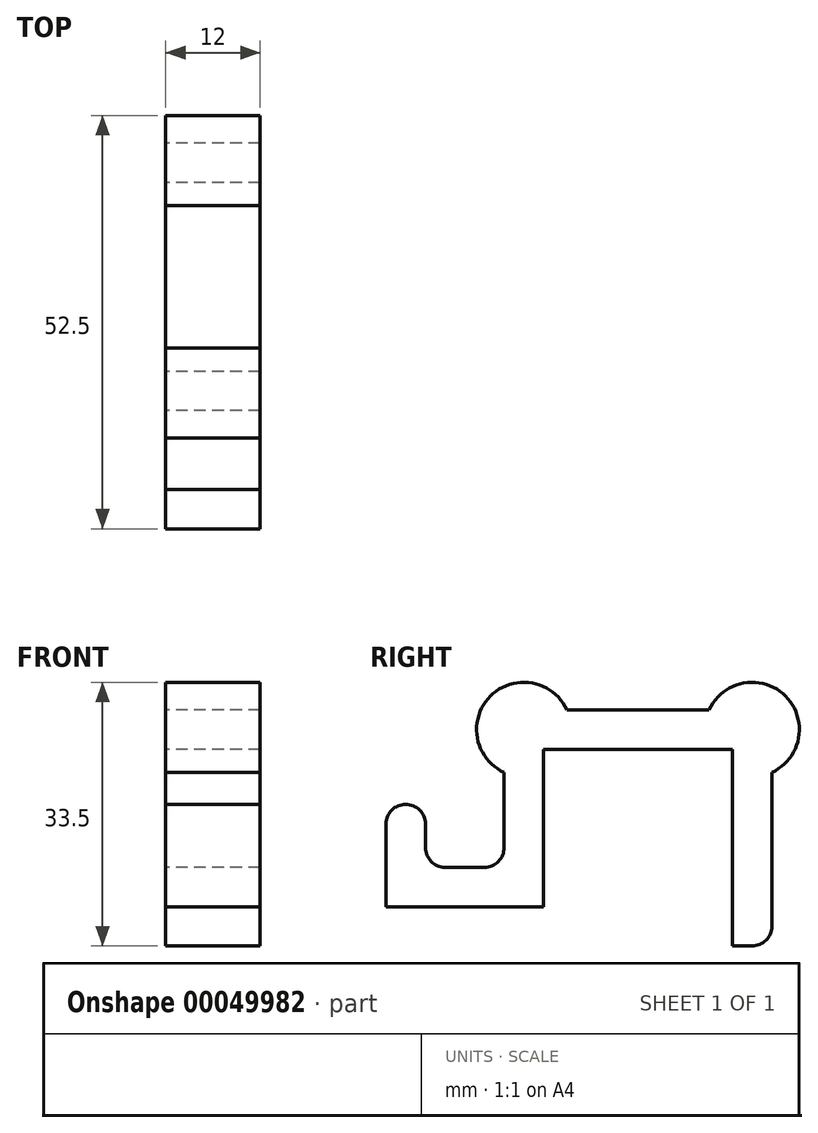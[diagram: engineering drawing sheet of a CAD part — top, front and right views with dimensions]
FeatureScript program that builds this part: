
annotation { "Feature Type Name" : "Feature", "Feature Type Description" : "" }
export const myFeature = defineFeature(function(context is Context, id is Id, definition is map)
    precondition{}
    {
        {
            var Q0;
            Q0=qCreatedBy(makeId("Right.planeOp"),FACE);
            var sketch = newSketch(context, id + "F0", { "sketchPlane" : qUnion([Q0])});
            skLineSegment(sketch, "E0", {"start": v(0, 0) * mm, "end": v(0, 20) * mm});
            skLineSegment(sketch, "E1", {"start": v(0, 20) * mm, "end": v(24, 20) * mm});
            skLineSegment(sketch, "E2", {"start": v(24, 20) * mm, "end": v(24, -5) * mm});
            skLineSegment(sketch, "E3", {"start": v(24, -5) * mm, "end": v(29, -5) * mm});
            skLineSegment(sketch, "E4", {"start": v(29, -5) * mm, "end": v(29, 25) * mm});
            skLineSegment(sketch, "E5", {"start": v(29, 25) * mm, "end": v(-5, 25) * mm});
            skLineSegment(sketch, "E6", {"start": v(-5, 25) * mm, "end": v(-5, 5) * mm});
            skLineSegment(sketch, "E7", {"start": v(-5, 5) * mm, "end": v(-15, 5) * mm});
            skLineSegment(sketch, "E8", {"start": v(-15, 5) * mm, "end": v(-15, 13) * mm});
            skLineSegment(sketch, "E9", {"start": v(-15, 13) * mm, "end": v(-20, 13) * mm});
            skLineSegment(sketch, "E10", {"start": v(-20, 13) * mm, "end": v(-20, 0) * mm});
            skLineSegment(sketch, "E11", {"start": v(-20, 0) * mm, "end": v(0, 0) * mm});
            skLineSegment(sketch, "E12", {"start": v(-5, 25) * mm, "end": v(0, 20) * mm});
            skLineSegment(sketch, "E13", {"start": v(29, 25) * mm, "end": v(24, 20) * mm});
            skArc(sketch, "E14", {"start": v(2.95, 25) * mm, "mid": v(-6.74, 26.74) * mm, "end": v(-5, 17.05) * mm});
            skArc(sketch, "E15", {"start": v(21.05, 25) * mm, "mid": v(30.74, 26.74) * mm, "end": v(29, 17.05) * mm});
            skSolve(sketch);
        }
        {
            var Q0;
            Q0 = qSketchRegion(id + "F0", true);
            extrude(context, id + "F1", {"entities" : qUnion([Q0]), "depth" : 12 * mm});
        }
        {
            var Q0;
            Q0=makeQuery(id+"F1.opExtrude","SWEPT_EDGE",EDGE,{"disambiguationData":[OSD([sQuery(id+"F0.wireOp",EDGE,"E6"),sQuery(id+"F0.wireOp",EDGE,"E7")])]});
            var Q1;
            Q1=makeQuery(id+"F1.opExtrude","SWEPT_EDGE",EDGE,{"disambiguationData":[OSD([sQuery(id+"F0.wireOp",EDGE,"E7"),sQuery(id+"F0.wireOp",EDGE,"E8")])]});
            var Q2;
            Q2=makeQuery(id+"F1.opExtrude","SWEPT_EDGE",EDGE,{"disambiguationData":[OSD([sQuery(id+"F0.wireOp",EDGE,"E3"),sQuery(id+"F0.wireOp",EDGE,"E4")])]});
            var Q3;
            Q3=makeQuery(id+"F1.opExtrude","SWEPT_EDGE",EDGE,{"disambiguationData":[OSD([sQuery(id+"F0.wireOp",EDGE,"E9"),sQuery(id+"F0.wireOp",EDGE,"E10")])]});
            var Q4;
            Q4=makeQuery(id+"F1.opExtrude","SWEPT_EDGE",EDGE,{"disambiguationData":[OSD([sQuery(id+"F0.wireOp",EDGE,"E8"),sQuery(id+"F0.wireOp",EDGE,"E9")])]});
            fillet(context, id + "F2", {"entities" : qUnion([Q0, Q1, Q2, Q3, Q4]), "radius" : 2.5 * mm, "allowEdgeOverflow" : false});
        }
    });
